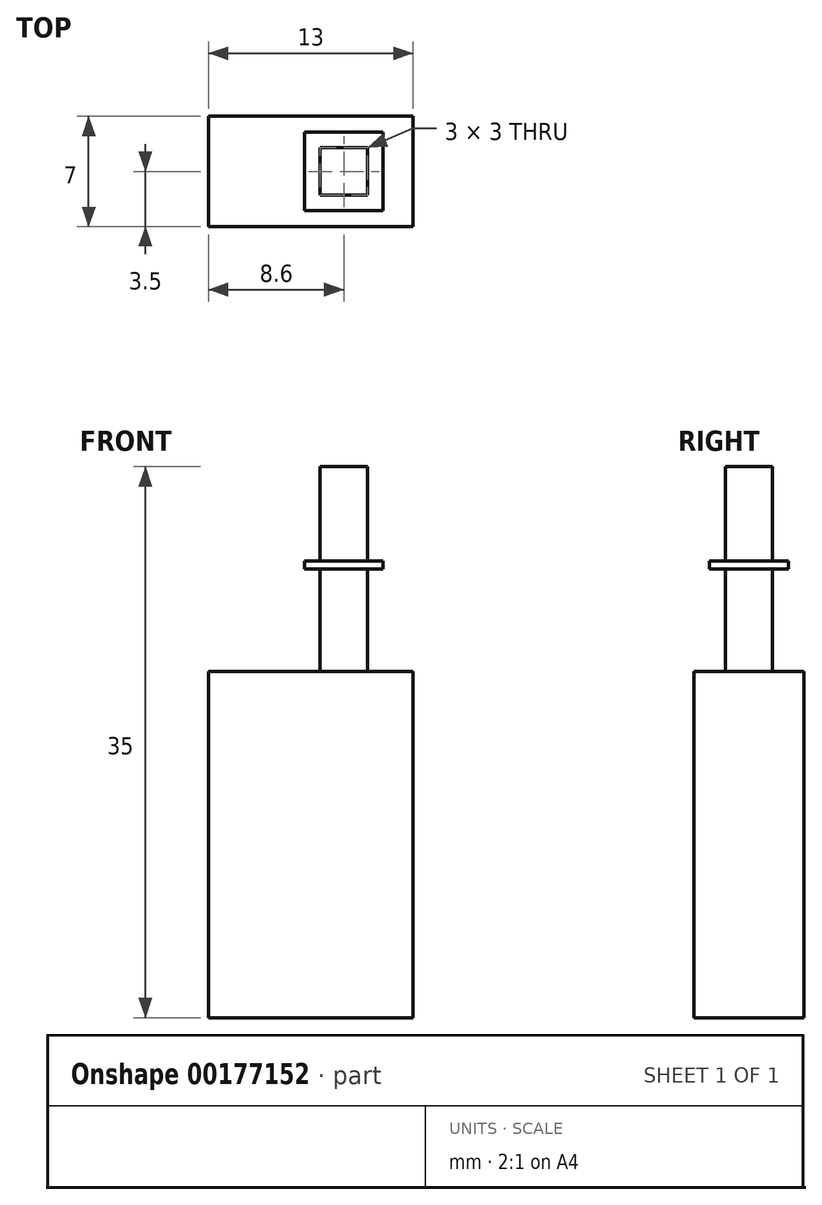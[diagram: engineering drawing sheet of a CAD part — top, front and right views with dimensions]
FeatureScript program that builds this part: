
annotation { "Feature Type Name" : "Feature", "Feature Type Description" : "" }
export const myFeature = defineFeature(function(context is Context, id is Id, definition is map)
    precondition{}
    {
        {
            var Q0;
            Q0=qCreatedBy(makeId("Top.planeOp"),FACE);
            var sketch = newSketch(context, id + "F0", { "sketchPlane" : qUnion([Q0])});
            skLineSegment(sketch, "E0.bottom", {"start": v(6.5, -3.5) * mm, "end": v(-6.5, -3.5) * mm});
            skLineSegment(sketch, "E0.top", {"start": v(6.5, 3.5) * mm, "end": v(-6.5, 3.5) * mm});
            skLineSegment(sketch, "E0.left", {"start": v(6.5, -3.5) * mm, "end": v(6.5, 3.5) * mm});
            skLineSegment(sketch, "E0.right", {"start": v(-6.5, -3.5) * mm, "end": v(-6.5, 3.5) * mm});
            skPoint(sketch, "E0.middle", {"position": v(0, 0) * mm});
            skSolve(sketch);
        }
        {
            var Q0;
            Q0 = qSketchRegion(id + "F0", true);
            extrude(context, id + "F1", {"entities" : qUnion([Q0]), "depth" : 22 * mm});
        }
        {
            var Q0;
            Q0=makeQuery(id+"F1.opExtrude","CAP_FACE",FACE,{"disambiguationData":[OSD([sQuery(id+"F0.wireOp",EDGE,"E0.bottom"),sQuery(id+"F0.wireOp",EDGE,"E0.top"),sQuery(id+"F0.wireOp",EDGE,"E0.left"),sQuery(id+"F0.wireOp",EDGE,"E0.right")])],"isStart":false});
            var sketch = newSketch(context, id + "F2", { "sketchPlane" : qUnion([Q0])});
            skLineSegment(sketch, "E1.bottom", {"start": v(3.6, -1.5) * mm, "end": v(0.6, -1.5) * mm});
            skLineSegment(sketch, "E1.top", {"start": v(3.6, 1.5) * mm, "end": v(0.6, 1.5) * mm});
            skLineSegment(sketch, "E1.left", {"start": v(3.6, -1.5) * mm, "end": v(3.6, 1.5) * mm});
            skLineSegment(sketch, "E1.right", {"start": v(0.6, -1.5) * mm, "end": v(0.6, 1.5) * mm});
            skPoint(sketch, "E1.middle", {"position": v(2.1, 0) * mm});
            skSolve(sketch);
        }
        {
            var Q0;
            Q0 = qSketchRegion(id + "F2", true);
            extrude(context, id + "F3", {"entities" : qUnion([Q0]), "depth" : 13 * mm});
        }
        {
            var Q0;
            Q0=makeQuery(id+"F3.opExtrude","CAP_FACE",FACE,{"disambiguationData":[OSD([sQuery(id+"F2.wireOp",EDGE,"E1.bottom"),sQuery(id+"F2.wireOp",EDGE,"E1.top"),sQuery(id+"F2.wireOp",EDGE,"E1.left"),sQuery(id+"F2.wireOp",EDGE,"E1.right")])],"isStart":false});
            cPlane(context, id + "F4", {"entities" : qUnion([Q0]), "cplaneType" : CPlaneType.OFFSET, "offset" : 6 * mm, "oppositeDirection" : true, "width" : 150 * mm, "height" : 150 * mm});
        }
        {
            var Q0;
            Q0=qCreatedBy(id+"F4.planeOp",FACE);
            var sketch = newSketch(context, id + "F5", { "sketchPlane" : qUnion([Q0])});
            skLineSegment(sketch, "E2.bottom", {"start": v(4.6, -2.5) * mm, "end": v(-0.4, -2.5) * mm});
            skLineSegment(sketch, "E2.top", {"start": v(4.6, 2.5) * mm, "end": v(-0.4, 2.5) * mm});
            skLineSegment(sketch, "E2.left", {"start": v(4.6, -2.5) * mm, "end": v(4.6, 2.5) * mm});
            skLineSegment(sketch, "E2.right", {"start": v(-0.4, -2.5) * mm, "end": v(-0.4, 2.5) * mm});
            skPoint(sketch, "E2.middle", {"position": v(2.1, 0) * mm});
            skSolve(sketch);
        }
        {
            var Q0;
            Q0 = qSketchRegion(id + "F5", true);
            extrude(context, id + "F6", {"entities" : qUnion([Q0]), "operationType" : NewBodyOperationType.ADD, "oppositeDirection" : true, "depth" : 0.5 * mm});
        }
    });
